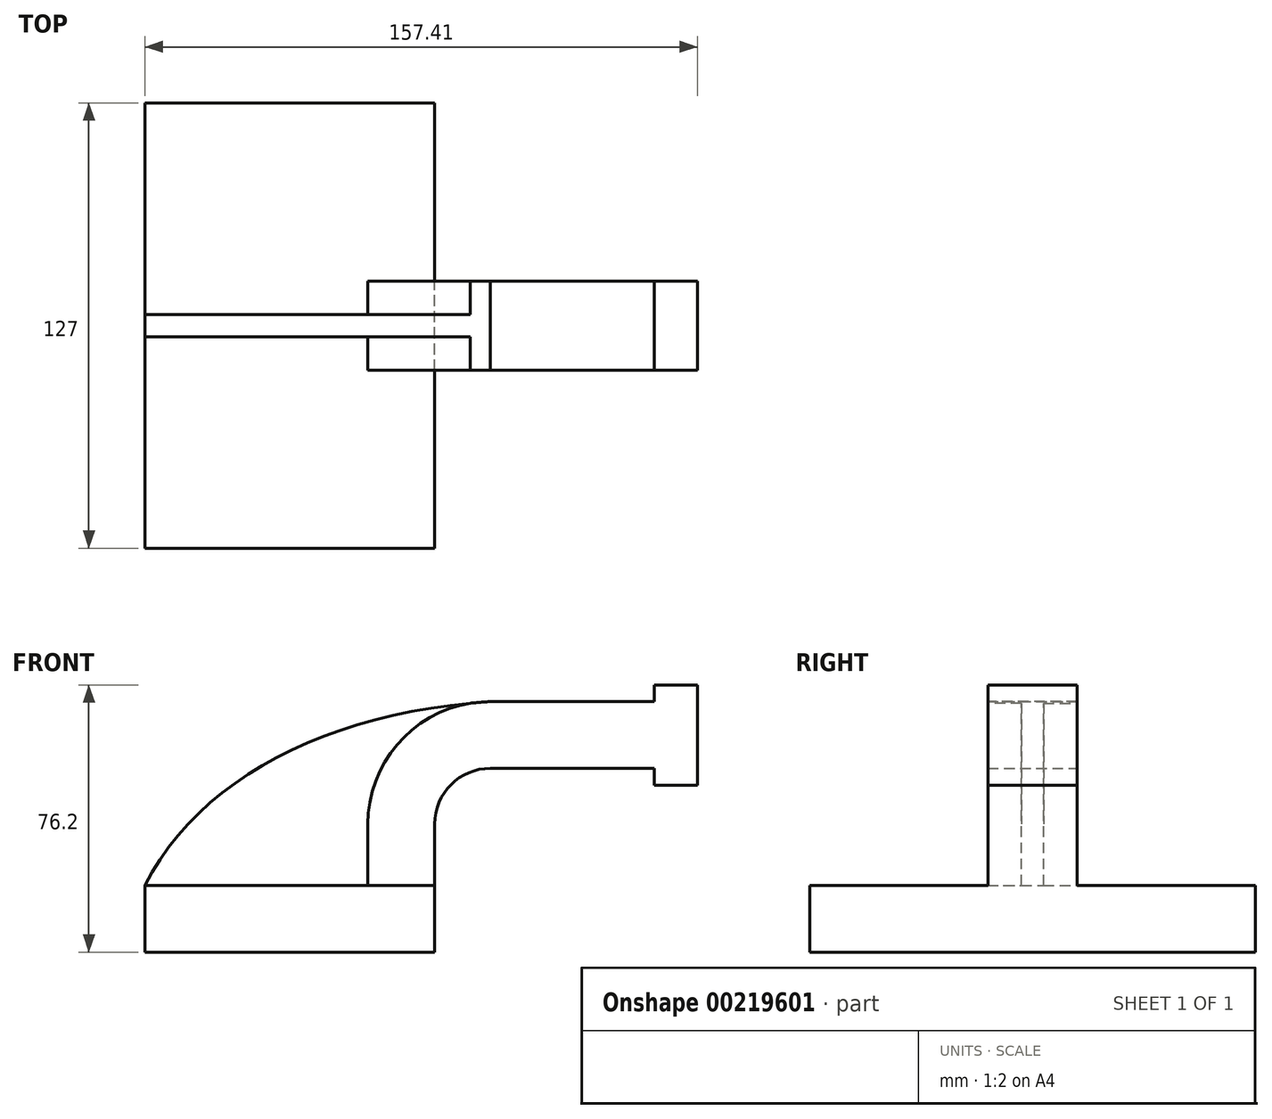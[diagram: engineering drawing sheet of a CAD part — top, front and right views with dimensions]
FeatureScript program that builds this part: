
annotation { "Feature Type Name" : "Feature", "Feature Type Description" : "" }
export const myFeature = defineFeature(function(context is Context, id is Id, definition is map)
    precondition{}
    {
        {
            var Q0;
            Q0=qCreatedBy(makeId("Front.planeOp"),FACE);
            var sketch = newSketch(context, id + "F0", { "sketchPlane" : qUnion([Q0])});
            skLineSegment(sketch, "E0.bottom", {"start": v(41.28, -9.52) * mm, "end": v(-41.28, -9.53) * mm});
            skLineSegment(sketch, "E0.top", {"start": v(41.28, 9.53) * mm, "end": v(-41.28, 9.53) * mm});
            skLineSegment(sketch, "E0.left", {"start": v(41.28, -9.52) * mm, "end": v(41.28, 9.53) * mm});
            skLineSegment(sketch, "E0.right", {"start": v(-41.28, -9.53) * mm, "end": v(-41.28, 9.53) * mm});
            skPoint(sketch, "E0.middle", {"position": v(0, 0) * mm});
            skLineSegment(sketch, "E1", {"start": v(41.28, 9.53) * mm, "end": v(41.28, 27) * mm});
            skLineSegment(sketch, "E2.bottom", {"start": v(65.33, 66.68) * mm, "end": v(116.13, 66.68) * mm});
            skLineSegment(sketch, "E2.top", {"start": v(65.33, 38.1) * mm, "end": v(116.13, 38.1) * mm});
            skLineSegment(sketch, "E2.left", {"start": v(65.33, 66.68) * mm, "end": v(65.33, 38.1) * mm});
            skLineSegment(sketch, "E2.right", {"start": v(116.13, 66.68) * mm, "end": v(116.13, 38.1) * mm});
            skArc(sketch, "E3", {"start": v(41.27, 27) * mm, "mid": v(45.92, 38.23) * mm, "end": v(57.15, 42.88) * mm});
            skPoint(sketch, "E3.endSnap0", {"position": v(65.33, 52.39) * mm});
            skLineSegment(sketch, "E4", {"start": v(57.15, 42.88) * mm, "end": v(103.8, 42.88) * mm});
            skLineSegment(sketch, "E5.0", {"start": v(57.15, 61.93) * mm, "end": v(103.8, 61.93) * mm});
            skArc(sketch, "E5.1", {"start": v(22.23, 27) * mm, "mid": v(32.45, 51.7) * mm, "end": v(57.15, 61.93) * mm});
            skLineSegment(sketch, "E5.2", {"start": v(22.23, 9.53) * mm, "end": v(22.23, 27) * mm});
            skFitSpline(sketch, "E6", {"points": [v(-41.28, 9.53) * mm, v(57.15, 61.93) * mm], "startDerivative": vector(45.97, 90.89) * mm, "endDerivative": vector(140.04, 9.45) * mm});
            skLineSegment(sketch, "E7", {"start": v(103.8, 66.68) * mm, "end": v(103.8, 38.1) * mm});
            skSolve(sketch);
        }
        {
            var Q0;
            Q0=makeQuery(id+"F0.imprint","IMPRINT",FACE,{"disambiguationData":[TD([[makeQuery(id+"F0.imprint","IMPRINT",EDGE,{"derivedFrom":sQuery(id+"F0.wireOp",EDGE,"E0.bottom")}),-1.0]])]});
            extrude(context, id + "F1", {"entities" : qUnion([Q0]), "endBound" : BoundingType.SYMMETRIC, "depth" : 127 * mm});
        }
        {
            var Q0;
            {var subQ6=sQuery(id+"F0.wireOp",EDGE,"E1");Q0=makeQuery(id+"F0.imprint","IMPRINT",FACE,{"disambiguationData":[TD([[makeQuery(id+"F0.imprint","IMPRINT",EDGE,{"derivedFrom":subQ6}),1.0]])]});}
            var Q1;
            {var subQ0=sQuery(id+"F0.wireOp",EDGE,"E2.right");Q1=makeQuery(id+"F0.imprint","IMPRINT",FACE,{"disambiguationData":[TD([[makeQuery(id+"F0.imprint","IMPRINT",EDGE,{"derivedFrom":subQ0}),-1.0]])]});}
            var Q2;
            {var subQ0=sQuery(id+"F0.wireOp",EDGE,"E5.0");var subQ1=sQuery(id+"F0.wireOp",EDGE,"E2.left");var subQ2=makeQuery(id+"F0.imprint","INTERSECT",VERTEX,{"derivedFrom":[subQ1,subQ0]});Q2=makeQuery(id+"F0.imprint","IMPRINT",FACE,{"disambiguationData":[TD([[makeQuery(id+"F0.imprint","IMPRINT",EDGE,{"disambiguationData":[TD([[subQ2,-1.0]])],"derivedFrom":subQ1}),1.0]])]});}
            extrude(context, id + "F2", {"entities" : qUnion([Q0, Q1, Q2]), "operationType" : NewBodyOperationType.ADD, "endBound" : BoundingType.SYMMETRIC, "depth" : 25.4 * mm});
        }
        {
            var Q0;
            {var subQ3=sQuery(id+"F0.wireOp",EDGE,"E5.2");Q0=makeQuery(id+"F0.imprint","IMPRINT",FACE,{"disambiguationData":[TD([[makeQuery(id+"F0.imprint","IMPRINT",EDGE,{"derivedFrom":subQ3}),1.0]])]});}
            extrude(context, id + "F3", {"entities" : qUnion([Q0]), "operationType" : NewBodyOperationType.ADD, "endBound" : BoundingType.SYMMETRIC, "depth" : 6.35 * mm});
        }
    });
